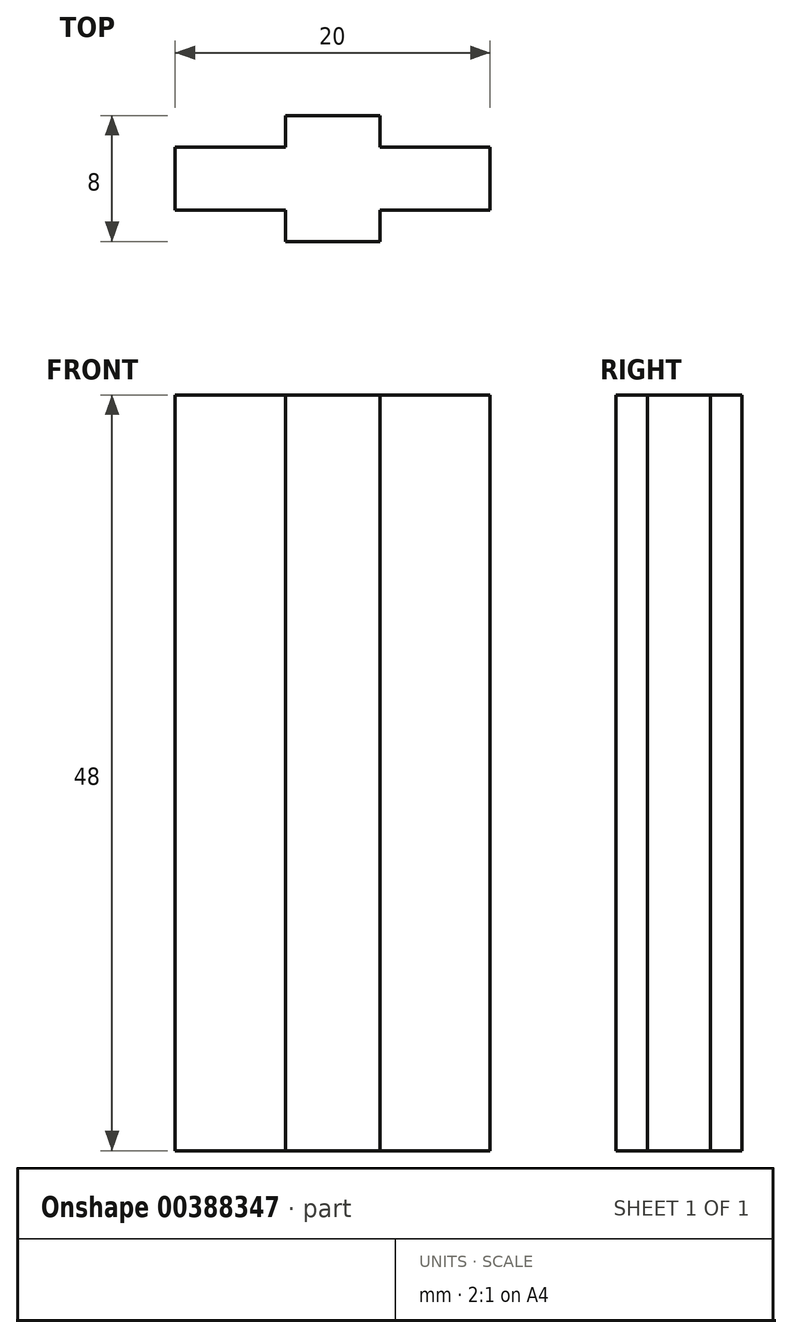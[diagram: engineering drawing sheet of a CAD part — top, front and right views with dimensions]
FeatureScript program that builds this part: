
annotation { "Feature Type Name" : "Feature", "Feature Type Description" : "" }
export const myFeature = defineFeature(function(context is Context, id is Id, definition is map)
    precondition{}
    {
        {
            var Q0;
            Q0=qCreatedBy(makeId("Top.planeOp"),FACE);
            var sketch = newSketch(context, id + "F0", { "sketchPlane" : qUnion([Q0])});
            skPoint(sketch, "E0.middle", {"position": v(0, 0) * mm});
            skLineSegment(sketch, "E1", {"start": v(0, 4) * mm, "end": v(3, 4) * mm});
            skLineSegment(sketch, "E2", {"start": v(0, 4) * mm, "end": v(-3, 4) * mm});
            skLineSegment(sketch, "E3", {"start": v(0, -4) * mm, "end": v(3, -4) * mm});
            skLineSegment(sketch, "E4", {"start": v(3, -4) * mm, "end": v(0, -4) * mm});
            skLineSegment(sketch, "E5", {"start": v(-3, -4) * mm, "end": v(0, -4) * mm});
            skLineSegment(sketch, "E6", {"start": v(10, 2) * mm, "end": v(3, 2) * mm});
            skLineSegment(sketch, "E7", {"start": v(3, -2) * mm, "end": v(10, -2) * mm});
            skLineSegment(sketch, "E8", {"start": v(3, 2) * mm, "end": v(3, 4) * mm});
            skLineSegment(sketch, "E9", {"start": v(3, -2) * mm, "end": v(3, -4) * mm});
            skLineSegment(sketch, "E10", {"start": v(-3, 2) * mm, "end": v(-10, 2) * mm});
            skLineSegment(sketch, "E11", {"start": v(-10, -2) * mm, "end": v(-3, -2) * mm});
            skLineSegment(sketch, "E12", {"start": v(-10, 2) * mm, "end": v(-10, -2) * mm});
            skLineSegment(sketch, "E13", {"start": v(10, -2) * mm, "end": v(10, 2) * mm});
            skLineSegment(sketch, "E14", {"start": v(-3, 4) * mm, "end": v(-3, 2) * mm});
            skLineSegment(sketch, "E15", {"start": v(-3, -4) * mm, "end": v(-3, -2) * mm});
            skSolve(sketch);
        }
        {
            var Q0;
            Q0=makeQuery(id+"F0.imprint","IMPRINT",FACE,{"disambiguationData":[TD([[makeQuery(id+"F0.imprint","IMPRINT",EDGE,{"derivedFrom":sQuery(id+"F0.wireOp",EDGE,"E1")}),-1.0]])]});
            extrude(context, id + "F1", {"entities" : qUnion([Q0]), "depth" : 48 * mm});
        }
    });
